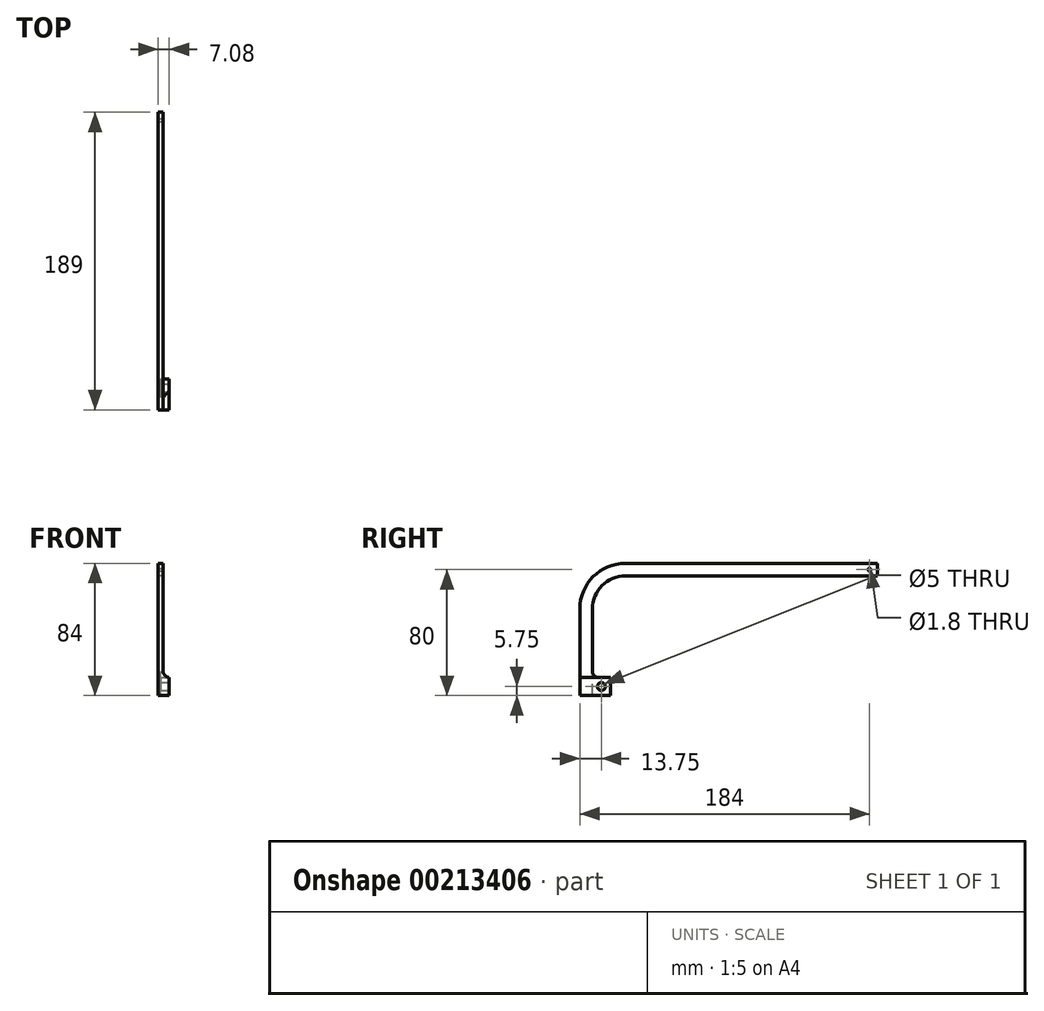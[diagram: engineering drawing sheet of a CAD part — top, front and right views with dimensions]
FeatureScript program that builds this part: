
annotation { "Feature Type Name" : "Feature", "Feature Type Description" : "" }
export const myFeature = defineFeature(function(context is Context, id is Id, definition is map)
    precondition{}
    {
        {
            var Q0;
            Q0=qCreatedBy(makeId("Right.planeOp"),FACE);
            var sketch = newSketch(context, id + "F0", { "sketchPlane" : qUnion([Q0])});
            skLineSegment(sketch, "E0", {"start": v(0, 0) * mm, "end": v(-185, 0) * mm, "construction": true});
            skLineSegment(sketch, "E1", {"start": v(-185, 0) * mm, "end": v(-185, -80) * mm, "construction": true});
            skSolve(sketch);
        }
        {
            var Q0;
            Q0=qCreatedBy(makeId("Right.planeOp"),FACE);
            var sketch = newSketch(context, id + "F1", { "sketchPlane" : qUnion([Q0])});
            skLineSegment(sketch, "E2.0", {"start": v(0, 0) * mm, "end": v(-160, 0) * mm});
            skLineSegment(sketch, "E2.1", {"start": v(-185, -25) * mm, "end": v(-185, -80) * mm});
            skPoint(sketch, "E3.visualSharp", {"position": v(-185, 0) * mm});
            skArc(sketch, "E3.filletArc", {"start": v(-160, 0) * mm, "mid": v(-177.68, -7.32) * mm, "end": v(-185, -25) * mm});
            skSolve(sketch);
        }
        {
            var Q0;
            Q0=qCreatedBy(makeId("Front.planeOp"),FACE);
            var sketch = newSketch(context, id + "F2", { "sketchPlane" : qUnion([Q0])});
            skLineSegment(sketch, "E4.bottom", {"start": v(1.57, -4) * mm, "end": v(-1.58, -4) * mm});
            skLineSegment(sketch, "E4.top", {"start": v(1.58, 4) * mm, "end": v(-1.57, 4) * mm});
            skLineSegment(sketch, "E4.left", {"start": v(1.57, -4) * mm, "end": v(1.58, 4) * mm});
            skLineSegment(sketch, "E4.right", {"start": v(-1.58, -4) * mm, "end": v(-1.57, 4) * mm});
            skPoint(sketch, "E4.middle", {"position": v(0, 0) * mm});
            skSolve(sketch);
        }
        {
            var Q0;
            Q0 = qSketchRegion(id + "F2", true);
            var Q1;
            Q1 = qConstructionFilter(qBodyType(qCreatedBy(id + "F1" ,EDGE), BodyType.WIRE), ConstructionObject.NO);
            sweep(context, id + "F3", {"profiles" : qUnion([Q0]), "path" : qUnion([Q1])});
        }
        {
            var Q0;
            Q0=makeQuery(id+"F3.opSweep","CAP_FACE",FACE,{"disambiguationData":[OSD([sQuery(id+"F1.wireOp",VERTEX,"E2.1.end"),sQuery(id+"F2.wireOp",EDGE,"E4.bottom"),sQuery(id+"F2.wireOp",EDGE,"E4.top"),sQuery(id+"F2.wireOp",EDGE,"E4.left"),sQuery(id+"F2.wireOp",EDGE,"E4.right")])],"isStart":false});
            var sketch = newSketch(context, id + "F4", { "sketchPlane" : qUnion([Q0])});
            skLineSegment(sketch, "E5.bottom", {"start": v(0, 189) * mm, "end": v(5.5, 189) * mm});
            skLineSegment(sketch, "E5.top", {"start": v(0, 169.5) * mm, "end": v(5.5, 169.5) * mm});
            skLineSegment(sketch, "E5.left", {"start": v(0, 189) * mm, "end": v(0, 169.5) * mm});
            skLineSegment(sketch, "E5.right", {"start": v(5.5, 189) * mm, "end": v(5.5, 169.5) * mm});
            skSolve(sketch);
        }
        {
            var Q0;
            Q0 = qSketchRegion(id + "F4", true);
            extrude(context, id + "F5", {"entities" : qUnion([Q0]), "operationType" : NewBodyOperationType.ADD, "oppositeDirection" : true, "depth" : 11.5 * mm});
        }
        {
            var Q0;
            Q0=makeQuery(id+"F5.opExtrude","SWEPT_FACE",FACE,{"disambiguationData":[OSD([sQuery(id+"F4.wireOp",EDGE,"E5.right")])]});
            var sketch = newSketch(context, id + "F6", { "sketchPlane" : qUnion([Q0])});
            skLineSegment(sketch, "E6", {"start": v(-169.5, -80) * mm, "end": v(-181, -68.5) * mm, "construction": true});
            skCircle(sketch, "E7", {"center": v(-175.25, -74.25) * mm, "radius": 2.5 * mm});
            skSolve(sketch);
        }
        {
            var Q0;
            Q0 = qSketchRegion(id + "F6", true);
            extrude(context, id + "F7", {"entities" : qUnion([Q0]), "operationType" : NewBodyOperationType.REMOVE, "endBound" : BoundingType.UP_TO_NEXT, "oppositeDirection" : true, "depth" : 25 * mm});
        }
        {
            var Q0;
            Q0=makeQuery(id+"F5.boolean.opBoolean","INTERSECT",EDGE,{"derivedFrom":[makeQuery(id+"F3.opSweep","SWEPT_FACE",FACE,{"disambiguationData":[OSD([sQuery(id+"F1.wireOp",EDGE,"E2.0"),sQuery(id+"F2.wireOp",EDGE,"E4.left")])]}),makeQuery(id+"F5.opExtrude","CAP_FACE",FACE,{"disambiguationData":[OSD([sQuery(id+"F4.wireOp",EDGE,"E5.bottom"),sQuery(id+"F4.wireOp",EDGE,"E5.top"),sQuery(id+"F4.wireOp",EDGE,"E5.left"),sQuery(id+"F4.wireOp",EDGE,"E5.right")])],"isStart":false})]});
            var Q1;
            Q1=makeQuery(id+"F5.boolean.opBoolean","INTERSECT",EDGE,{"derivedFrom":[makeQuery(id+"F3.opSweep","SWEPT_FACE",FACE,{"disambiguationData":[OSD([sQuery(id+"F1.wireOp",EDGE,"E2.1"),sQuery(id+"F2.wireOp",EDGE,"E4.bottom")])]}),makeQuery(id+"F5.opExtrude","CAP_FACE",FACE,{"disambiguationData":[OSD([sQuery(id+"F4.wireOp",EDGE,"E5.bottom"),sQuery(id+"F4.wireOp",EDGE,"E5.top"),sQuery(id+"F4.wireOp",EDGE,"E5.left"),sQuery(id+"F4.wireOp",EDGE,"E5.right")])],"isStart":false})]});
            fillet(context, id + "F8", {"entities" : qUnion([Q0, Q1]), "radius" : 4 * mm, "tangentPropagation" : true, "allowEdgeOverflow" : false});
        }
        {
            var Q0;
            Q0=makeQuery(id+"F3.opSweep","SWEPT_FACE",FACE,{"disambiguationData":[OSD([sQuery(id+"F1.wireOp",EDGE,"E2.0"),sQuery(id+"F2.wireOp",EDGE,"E4.left")])]});
            var sketch = newSketch(context, id + "F9", { "sketchPlane" : qUnion([Q0])});
            skLineSegment(sketch, "E8", {"start": v(0, 0) * mm, "end": v(-5, 0) * mm, "construction": true});
            skCircle(sketch, "E9", {"center": v(-5, 0) * mm, "radius": 0.9 * mm});
            skSolve(sketch);
        }
        {
            var Q0;
            Q0 = qSketchRegion(id + "F9", true);
            extrude(context, id + "F10", {"entities" : qUnion([Q0]), "operationType" : NewBodyOperationType.REMOVE, "endBound" : BoundingType.UP_TO_NEXT, "oppositeDirection" : true, "depth" : 25 * mm});
        }
    });
